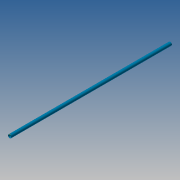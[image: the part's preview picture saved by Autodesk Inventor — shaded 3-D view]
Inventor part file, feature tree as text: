
AUTODESK INVENTOR PART (.ipt)
format: ipt  version: 2014 SP1 (Build 180222100, 222)  size: 98,304 bytes
history: native  units: in
note: dims shown in document units (in); Inventor stores cm internally (conversion verified against a paired STEP export)
features: sketch x4, extrude x2, plane x2, hole x1, other x1
ambient origin geometry x8: Origin, YZ Plane, XZ Plane, XY Plane, X Axis, Y Axis, Z Axis, Center Point
bodies: Solid1 (feature_tree)
feature tree (10):
  extrude  "Extrusion1"  Depth=0.1417in
  sketch  "Sketch4"  dims[d3=118.1102in d4=0.0in d16=0.7874in]
  plane  "Work Plane2"
  hole  "Hole2"  [1 undecoded]
  other  "Work Point1"
  plane  "Work Plane3"
  extrude  "Extrusion2"  Depth=1.1811in
  sketch  "Sketch1"  dims[d0=2.4803in d2=0.1417in]
  sketch  "Sketch5"  dims[d18=0.125in d19=0.75in d20=0.375in d21=0.25in d22=0.5635in d23=1.0in d24=0.8108in d25=1.1811in]
  sketch  "Sketch6"  dims[d26=1.0in d27=0.0in]
note: 1 required parameter value undecoded (feature->parameter linkage not recoverable at this tier; creation-order binding heuristic only, values carry confidence <= 0.55)
